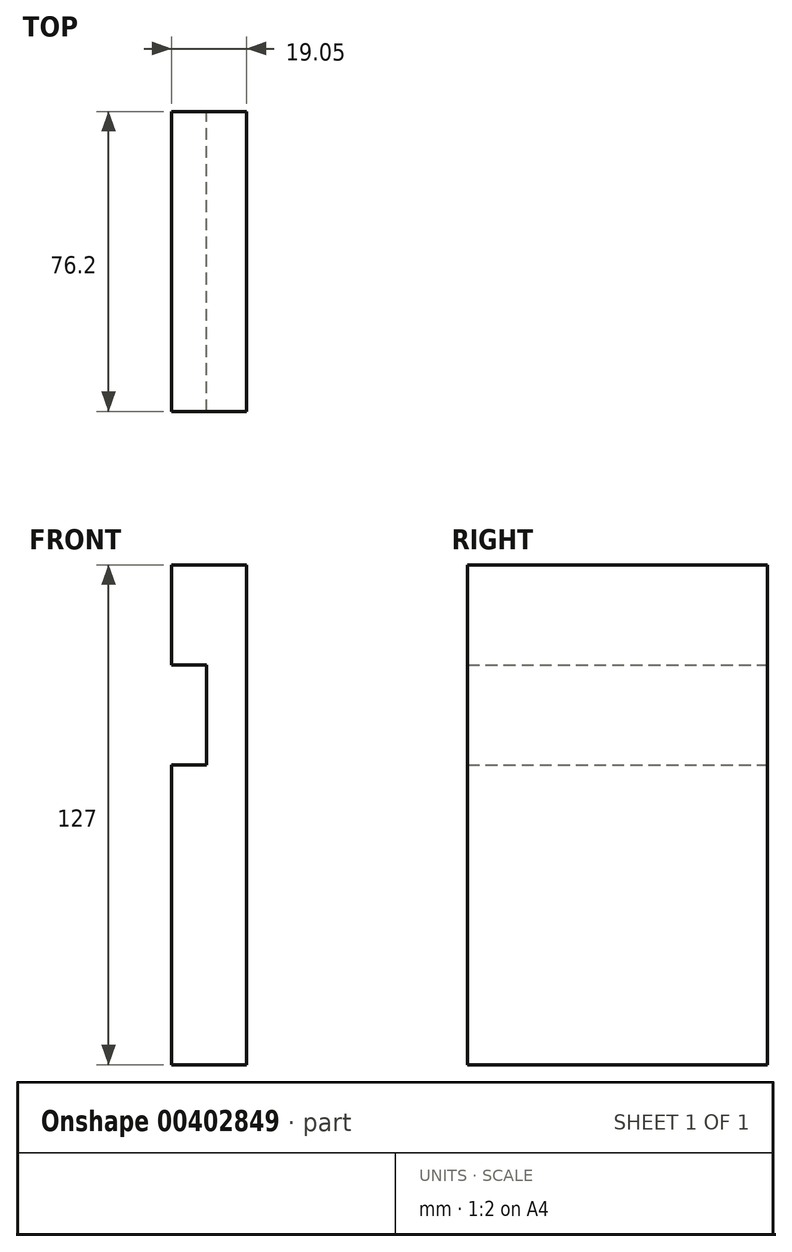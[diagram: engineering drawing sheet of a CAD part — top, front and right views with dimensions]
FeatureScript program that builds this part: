
annotation { "Feature Type Name" : "Feature", "Feature Type Description" : "" }
export const myFeature = defineFeature(function(context is Context, id is Id, definition is map)
    precondition{}
    {
        {
            var Q0;
            Q0=qCreatedBy(makeId("Front.planeOp"),FACE);
            var sketch = newSketch(context, id + "F0", { "sketchPlane" : qUnion([Q0])});
            skLineSegment(sketch, "E0", {"start": v(0, -72.16) * mm, "end": v(0, 54.84) * mm});
            skLineSegment(sketch, "E1", {"start": v(0, 54.84) * mm, "end": v(-19.05, 54.84) * mm});
            skLineSegment(sketch, "E2", {"start": v(-19.05, 54.84) * mm, "end": v(-19.05, 29.44) * mm});
            skLineSegment(sketch, "E3", {"start": v(-19.05, 29.44) * mm, "end": v(-10.16, 29.44) * mm});
            skLineSegment(sketch, "E4", {"start": v(-10.16, 29.44) * mm, "end": v(-10.16, 4.04) * mm});
            skLineSegment(sketch, "E5", {"start": v(-10.16, 4.04) * mm, "end": v(-19.05, 4.04) * mm});
            skLineSegment(sketch, "E6", {"start": v(0, -72.16) * mm, "end": v(-19.05, -72.16) * mm});
            skLineSegment(sketch, "E7", {"start": v(-19.05, -72.16) * mm, "end": v(-19.05, 4.04) * mm});
            skSolve(sketch);
        }
        {
            var Q0;
            Q0=makeQuery(id+"F0.imprint","IMPRINT",FACE,{"disambiguationData":[TD([[makeQuery(id+"F0.imprint","IMPRINT",EDGE,{"derivedFrom":sQuery(id+"F0.wireOp",EDGE,"E0")}),1.0]])]});
            extrude(context, id + "F1", {"entities" : qUnion([Q0]), "depth" : 76.2 * mm});
        }
    });
